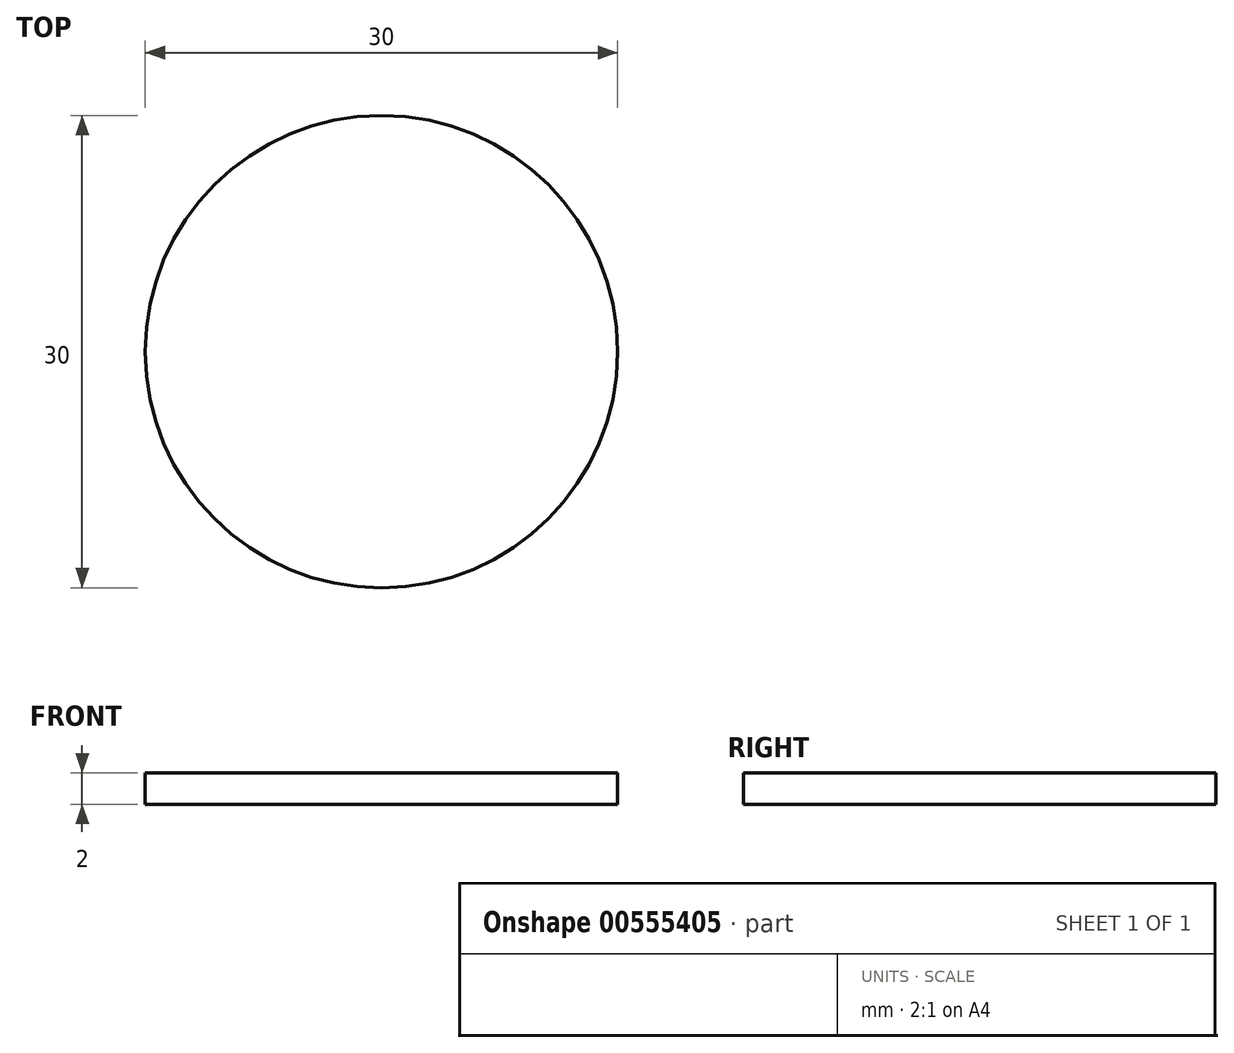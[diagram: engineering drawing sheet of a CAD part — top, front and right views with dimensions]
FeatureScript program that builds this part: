
annotation { "Feature Type Name" : "Feature", "Feature Type Description" : "" }
export const myFeature = defineFeature(function(context is Context, id is Id, definition is map)
    precondition{}
    {
        {
            var Q0;
            Q0=qCreatedBy(makeId("Top.planeOp"),FACE);
            var sketch = newSketch(context, id + "F0", { "sketchPlane" : qUnion([Q0])});
            skCircle(sketch, "E0", {"center": v(0, 0) * mm, "radius": 15 * mm});
            skSolve(sketch);
        }
        {
            var Q0;
            Q0 = qSketchRegion(id + "F0", true);
            extrude(context, id + "F1", {"entities" : qUnion([Q0]), "depth" : 2 * mm, "offsetDistance" : 25 * mm});
        }
    });
